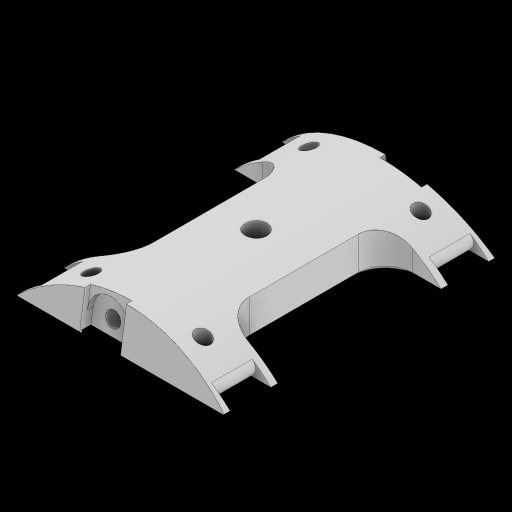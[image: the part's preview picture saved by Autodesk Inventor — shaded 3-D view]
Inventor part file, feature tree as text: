
AUTODESK INVENTOR PART (.ipt)
format: ipt  version: 2023 (Build 270158000, 158)  size: 401,408 bytes
history: native  units: mm
features: extrude x14, sketch x6, fillet x2, chamfer x1, plane x1, hole x1
ambient origin geometry x8: Origin, YZ Plane, XZ Plane, XY Plane, X Axis, Y Axis, Z Axis, Center Point
bodies: Solid1 (feature_tree)
feature tree (25):
  sketch  "Sketch1"  dims[d0=5.5mm d1=15.0mm d2=20.0mm]
  extrude  "Extrusion1"  Depth=20.0mm
  extrude  "Extrusion2"  Depth=17.0mm TaperAngle=0.0deg
  fillet  "Fillet2"  Radius=2.0mm
  chamfer  "Chamfer1"  Distance=200.0mm
  plane  "Work Plane1"
  extrude  "Extrusion3"  Depth=2.0mm
  extrude  "Extrusion4"  TaperAngle=90.0deg  [1 undecoded]
  extrude  "Extrusion5"  TaperAngle=90.0deg  [1 undecoded]
  extrude  "Extrusion6"  Depth=10.93871mm
  sketch  "Sketch4"  dims[d18=100.0mm d20=90.0deg]
  extrude  "Extrusion10"  Depth=2.0mm
  extrude  "Extrusion11"  Depth=200.0mm TaperAngle=0.0deg
  extrude  "Extrusion12"  Depth=2.0mm TaperAngle=0.0deg
  sketch  "Sketch5"  dims[d21=260.34779mm d22=90.0deg]
  extrude  "Extrusion13"  Depth=3.0mm TaperAngle=0.0deg
  extrude  "Extrusion14"  Depth=15.0mm TaperAngle=0.0deg
  extrude  "Extrusion15"  Depth=15.0mm
  hole  "Hole1"  [1 undecoded]
  fillet  "Fillet4"  Radius=2.0mm
  extrude  "Extrusion16"  TaperAngle=90.0deg  [1 undecoded]
  extrude  "Extrusion17"  Depth=15.0mm
  sketch  "Sketch2"  dims[d4=35.0mm d5=17.0mm d6=0.0mm d7=2.0mm d10=200.0mm d11=0.0mm]
  sketch  "Sketch3"  dims[d13=10.0mm d14=2.0mm d15=4.0mm d16=13.962634mm]
  sketch  "Sketch6"  dims[d23=47.979859mm d24=10.93871mm d25=2.0mm d26=200.0mm d27=0.0mm d28=2.0mm d29=0.0mm d30=3.0mm d31=0.0mm d32=15.0mm d33=0.0mm d35=15.0mm d36=90.0deg d37=2.0mm d38=90.0deg d39=15.0mm d40=15.0mm d41=5.5mm d42=20.0mm d49=4.0mm d50=0.0mm d51=2.0mm d52=2.0mm d53=0.0mm d54=20.0mm d55=0.0mm d56=15.0mm d57=90.0deg d58=2.0mm d59=90.0deg d60=15.0mm d61=15.0mm d62=5.5mm d63=20.0mm d64=2.0mm d65=2.0mm d66=0.0mm d67=4.0mm d68=0.0mm d69=20.0mm d70=0.0mm d72=8.0mm d73=6.0mm d74=20.0mm d75=2.0mm d76=90.0deg d77=20.0mm d78=0.0mm d79=3.0mm d82=7.5mm d83=244.423mm d84=41.005864mm d85=18.0mm d86=264.926mm d87=0.0mm d88=15.0mm d89=2.0mm d90=0.0mm d91=1.0mm d92=0.0mm d8=0.872665mm d17=0.0mm d19=0.0mm d71=0.0mm d80=0.0mm d81=0.0mm]
note: 4 required parameter values undecoded (feature->parameter linkage not recoverable at this tier; creation-order binding heuristic only, values carry confidence <= 0.55)
